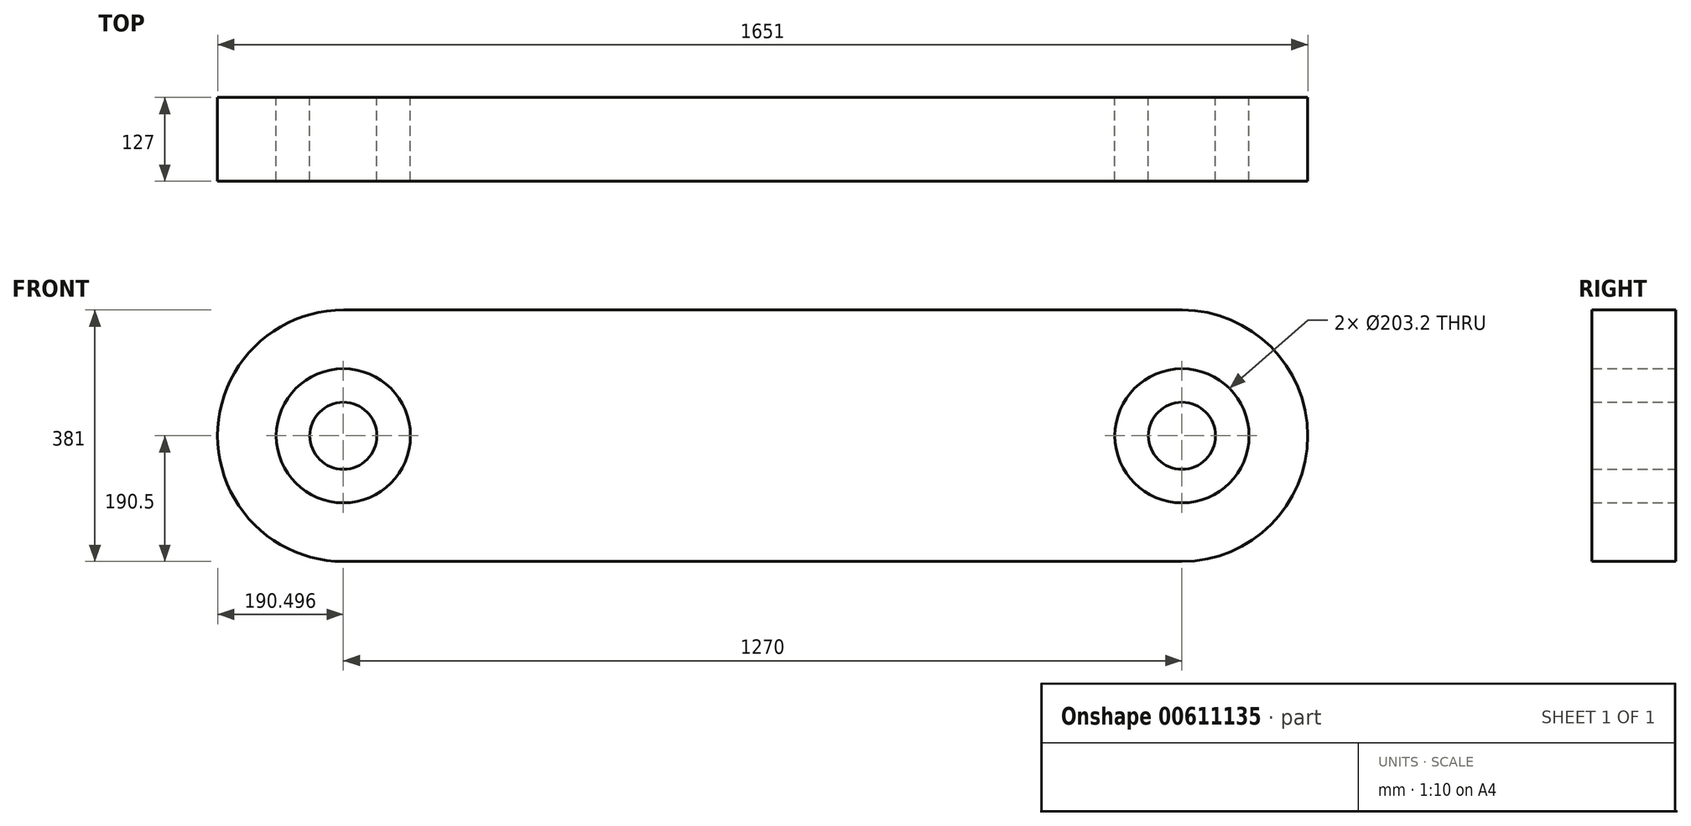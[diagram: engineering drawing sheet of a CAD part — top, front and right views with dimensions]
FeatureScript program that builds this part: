
annotation { "Feature Type Name" : "Feature", "Feature Type Description" : "" }
export const myFeature = defineFeature(function(context is Context, id is Id, definition is map)
    precondition{}
    {
        {
            var Q0;
            Q0=qCreatedBy(makeId("Front.planeOp"),FACE);
            var sketch = newSketch(context, id + "F0", { "sketchPlane" : qUnion([Q0])});
            skLineSegment(sketch, "E0.bottom", {"start": v(635, 190.5) * mm, "end": v(-635, 190.5) * mm});
            skLineSegment(sketch, "E0.top", {"start": v(635, -190.5) * mm, "end": v(-635, -190.5) * mm});
            skPoint(sketch, "E0.middle", {"position": v(0, 0) * mm});
            skArc(sketch, "E1", {"start": v(-635, 190.5) * mm, "mid": v(-825.5, 0) * mm, "end": v(-635, -190.5) * mm});
            skArc(sketch, "E2", {"start": v(635, -190.5) * mm, "mid": v(825.5, 0) * mm, "end": v(635, 190.5) * mm});
            skCircle(sketch, "E3", {"center": v(-635, 0) * mm, "radius": 101.6 * mm});
            skCircle(sketch, "E4", {"center": v(635, 0) * mm, "radius": 101.6 * mm});
            skCircle(sketch, "E5", {"center": v(-635, 0) * mm, "radius": 50.8 * mm});
            skCircle(sketch, "E6", {"center": v(635, 0) * mm, "radius": 50.8 * mm});
            skSolve(sketch);
        }
        {
            var Q0;
            Q0=makeQuery(id+"F0.imprint","IMPRINT",FACE,{"disambiguationData":[TD([[makeQuery(id+"F0.imprint","IMPRINT",EDGE,{"derivedFrom":sQuery(id+"F0.wireOp",EDGE,"E0.bottom")}),1.0]])]});
            var Q1;
            Q1=makeQuery(id+"F0.imprint","IMPRINT",FACE,{"disambiguationData":[TD([[makeQuery(id+"F0.imprint","IMPRINT",EDGE,{"derivedFrom":sQuery(id+"F0.wireOp",EDGE,"E5")}),1.0]])]});
            var Q2;
            Q2=makeQuery(id+"F0.imprint","IMPRINT",FACE,{"disambiguationData":[TD([[makeQuery(id+"F0.imprint","IMPRINT",EDGE,{"derivedFrom":sQuery(id+"F0.wireOp",EDGE,"E6")}),1.0]])]});
            extrude(context, id + "F1", {"entities" : qUnion([Q0, Q1, Q2]), "endBound" : BoundingType.SYMMETRIC, "depth" : 127 * mm, "offsetDistance" : 25.4 * mm});
        }
    });
